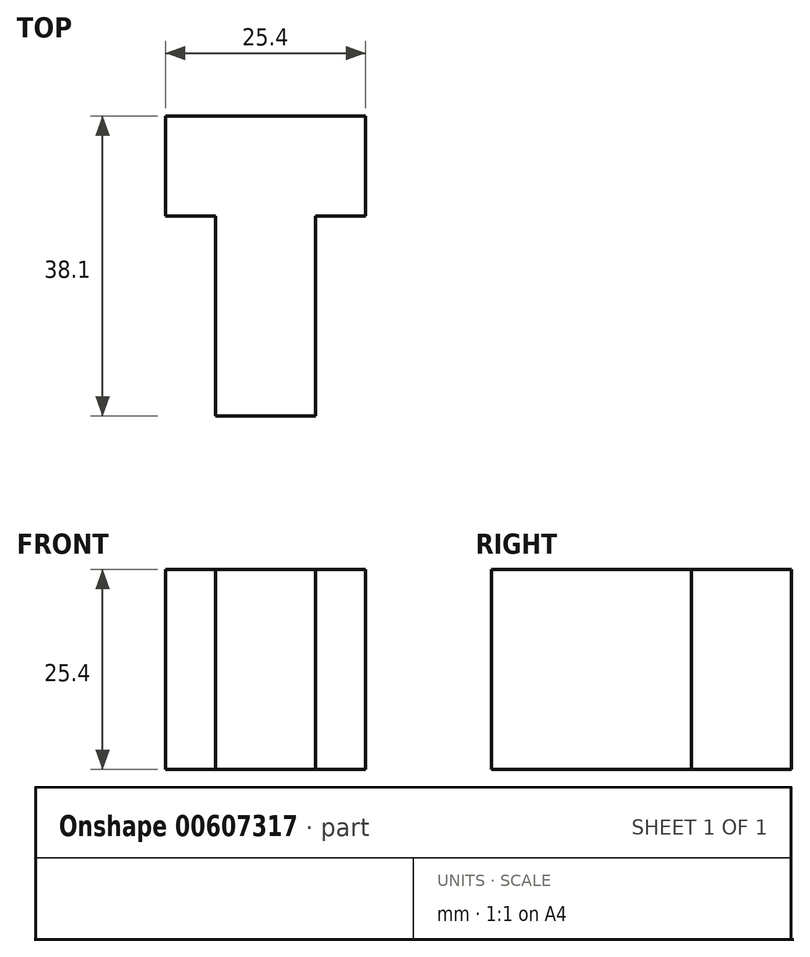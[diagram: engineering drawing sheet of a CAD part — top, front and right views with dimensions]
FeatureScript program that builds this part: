
annotation { "Feature Type Name" : "Feature", "Feature Type Description" : "" }
export const myFeature = defineFeature(function(context is Context, id is Id, definition is map)
    precondition{}
    {
        {
            var Q0;
            Q0=qCreatedBy(makeId("Top.planeOp"),FACE);
            var sketch = newSketch(context, id + "F0", { "sketchPlane" : qUnion([Q0])});
            skLineSegment(sketch, "E0", {"start": v(0, 0) * mm, "end": v(-6.35, 0) * mm});
            skLineSegment(sketch, "E1", {"start": v(-6.35, 0) * mm, "end": v(-6.35, 25.4) * mm});
            skLineSegment(sketch, "E2", {"start": v(-6.35, 25.4) * mm, "end": v(-12.7, 25.4) * mm});
            skLineSegment(sketch, "E3", {"start": v(-12.7, 25.4) * mm, "end": v(-12.7, 38.1) * mm});
            skLineSegment(sketch, "E4", {"start": v(-12.7, 38.1) * mm, "end": v(12.7, 38.1) * mm});
            skLineSegment(sketch, "E5", {"start": v(12.7, 38.1) * mm, "end": v(12.7, 25.4) * mm});
            skLineSegment(sketch, "E6", {"start": v(12.7, 25.4) * mm, "end": v(6.35, 25.4) * mm});
            skLineSegment(sketch, "E7", {"start": v(6.35, 25.4) * mm, "end": v(6.35, 0) * mm});
            skLineSegment(sketch, "E8", {"start": v(0, 0) * mm, "end": v(6.35, 0) * mm});
            skSolve(sketch);
        }
        {
            var Q0;
            Q0=makeQuery(id+"F0.imprint","IMPRINT",FACE,{"disambiguationData":[TD([[makeQuery(id+"F0.imprint","IMPRINT",EDGE,{"derivedFrom":sQuery(id+"F0.wireOp",EDGE,"E0")}),-1.0]])]});
            extrude(context, id + "F1", {"entities" : qUnion([Q0]), "depth" : 25.4 * mm, "offsetDistance" : 25.4 * mm});
        }
    });
